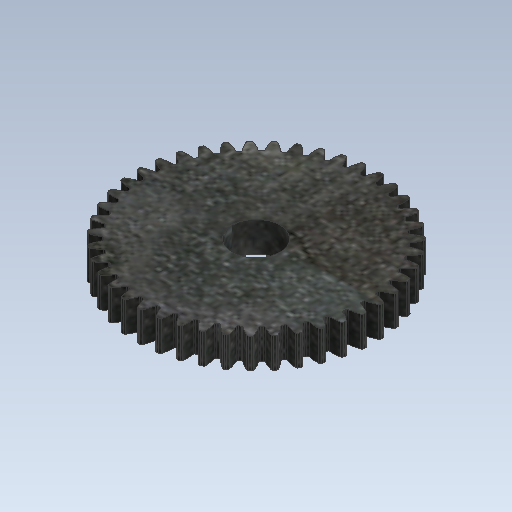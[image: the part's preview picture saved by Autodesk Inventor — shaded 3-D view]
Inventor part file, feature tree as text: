
AUTODESK INVENTOR PART (.ipt)
format: ipt  version: 2021 (Build 250183000, 183)  size: 622,592 bytes
history: native  units: mm
features: extrude x2, sketch x2, fillet x1, pattern_circular x1
ambient origin geometry x8: Origin, YZ Plane, XZ Plane, XY Plane, X Axis, Y Axis, Z Axis, Center Point
bodies: Solid1 (feature_tree)
feature tree (6):
  extrude  "Extrusion1"  Depth=7.0mm TaperAngle=360.0deg
  fillet  "Fillet2"  Radius=53.15mm
  pattern_circular  "Circular Pattern2"  [2 undecoded]
  extrude  "Extrusion3"  Depth=0.4mm
  sketch  "Sketch1"  dims[d4=7.0mm d5=0.0mm d18=430.0mm d19=360.0deg d23=53.15mm]
  sketch  "Sketch3"  dims[d25=1.545058mm d26=1.236047mm d27=3.490659mm d28=49.944663mm d29=3.490659mm d30=0.309012mm d31=0.618023mm d32=0.970791mm d33=0.4mm d34=11.0mm d35=3.0mm d36=0.0mm]
note: 2 required parameter values undecoded (feature->parameter linkage not recoverable at this tier; creation-order binding heuristic only, values carry confidence <= 0.55)
